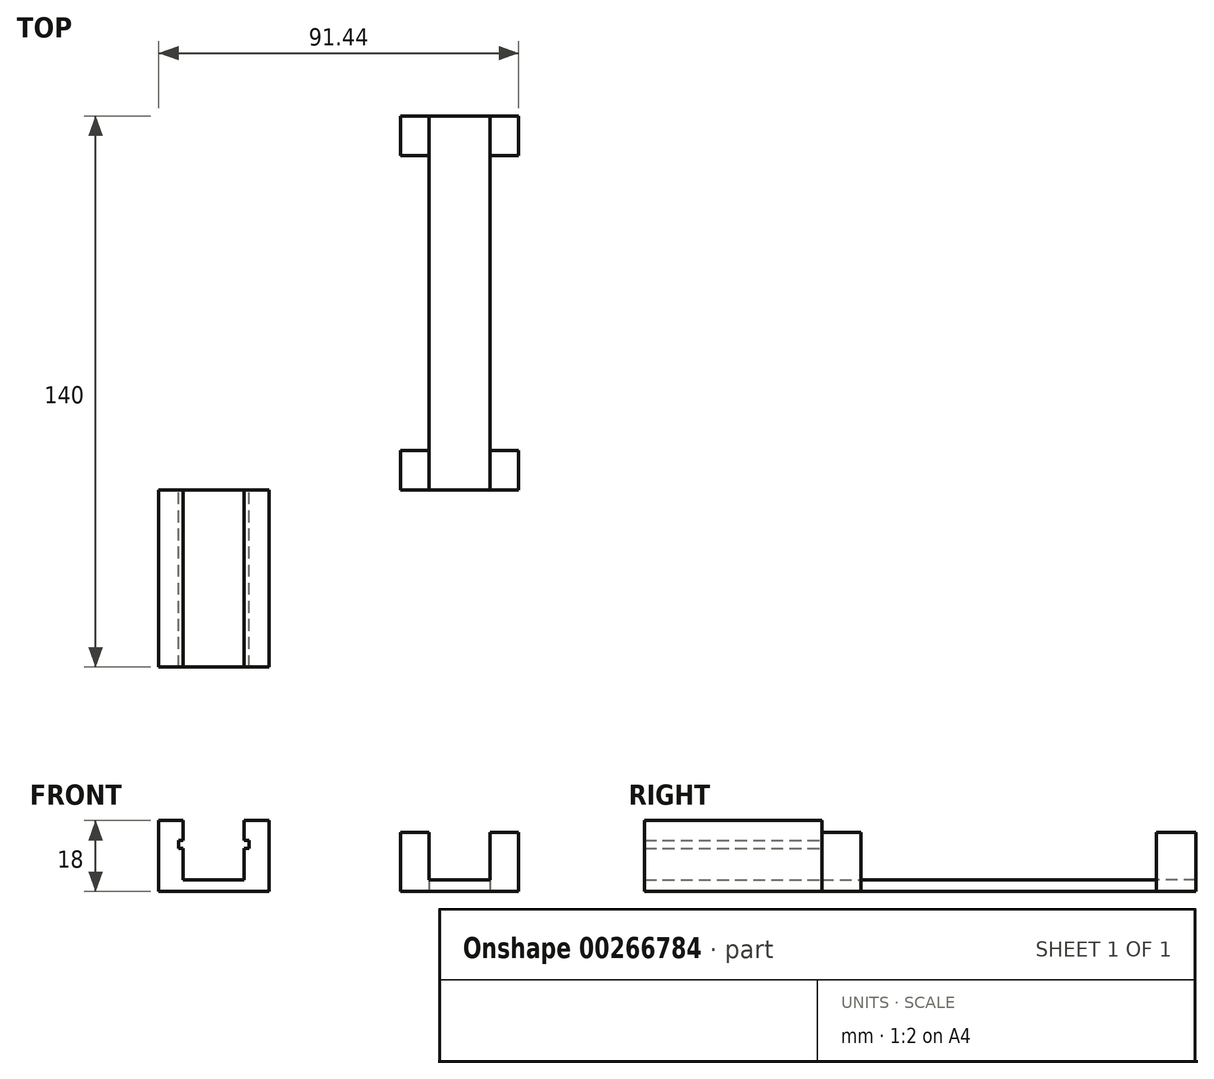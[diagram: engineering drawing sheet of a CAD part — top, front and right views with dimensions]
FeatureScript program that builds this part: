
annotation { "Feature Type Name" : "Feature", "Feature Type Description" : "" }
export const myFeature = defineFeature(function(context is Context, id is Id, definition is map)
    precondition{}
    {
        {
            var Q0;
            Q0=qCreatedBy(makeId("Top.planeOp"),FACE);
            var sketch = newSketch(context, id + "F0", { "sketchPlane" : qUnion([Q0])});
            skLineSegment(sketch, "E0", {"start": v(0, 0) * mm, "end": v(30, 0) * mm});
            skLineSegment(sketch, "E1", {"start": v(30, 0) * mm, "end": v(30, 10) * mm});
            skLineSegment(sketch, "E2", {"start": v(30, 95) * mm, "end": v(0, 95) * mm});
            skLineSegment(sketch, "E3", {"start": v(0, 95) * mm, "end": v(0, 85) * mm});
            skLineSegment(sketch, "E4", {"start": v(7.25, 0) * mm, "end": v(7.25, 10) * mm});
            skLineSegment(sketch, "E5", {"start": v(22.75, 95) * mm, "end": v(22.75, 85) * mm});
            skLineSegment(sketch, "E6", {"start": v(0, 10) * mm, "end": v(7.25, 10) * mm});
            skLineSegment(sketch, "E7", {"start": v(0, 85) * mm, "end": v(7.25, 85) * mm});
            skLineSegment(sketch, "E8.trimOffspring", {"start": v(7.25, 85) * mm, "end": v(7.25, 95) * mm});
            skLineSegment(sketch, "E9.trimOffspring", {"start": v(22.75, 10) * mm, "end": v(22.75, 0) * mm});
            skLineSegment(sketch, "E10.trimOffspring", {"start": v(22.75, 85) * mm, "end": v(30, 85) * mm});
            skLineSegment(sketch, "E11.trimOffspring", {"start": v(22.75, 10) * mm, "end": v(30, 10) * mm});
            skLineSegment(sketch, "E12", {"start": v(7.25, 10) * mm, "end": v(7.25, 85) * mm});
            skLineSegment(sketch, "E13", {"start": v(22.75, 10) * mm, "end": v(22.75, 85) * mm});
            skLineSegment(sketch, "E14.trimOffspring", {"start": v(0, 10) * mm, "end": v(0, 0) * mm});
            skLineSegment(sketch, "E15.trimOffspring", {"start": v(30, 85) * mm, "end": v(30, 95) * mm});
            skSolve(sketch);
        }
        {
            var Q0;
            {var subQ0=sQuery(id+"F0.wireOp",EDGE,"E3");Q0=makeQuery(id+"F0.imprint","IMPRINT",FACE,{"disambiguationData":[TD([[makeQuery(id+"F0.imprint","IMPRINT",EDGE,{"derivedFrom":subQ0}),1.0]])]});}
            var Q1;
            {var subQ0=sQuery(id+"F0.wireOp",EDGE,"E1");Q1=makeQuery(id+"F0.imprint","IMPRINT",FACE,{"disambiguationData":[TD([[makeQuery(id+"F0.imprint","IMPRINT",EDGE,{"derivedFrom":subQ0}),1.0]])]});}
            var Q2;
            {var subQ2=sQuery(id+"F0.wireOp",EDGE,"E5");Q2=makeQuery(id+"F0.imprint","IMPRINT",FACE,{"disambiguationData":[TD([[makeQuery(id+"F0.imprint","IMPRINT",EDGE,{"derivedFrom":subQ2}),1.0]])]});}
            var Q3;
            {var subQ2=sQuery(id+"F0.wireOp",EDGE,"E4");Q3=makeQuery(id+"F0.imprint","IMPRINT",FACE,{"disambiguationData":[TD([[makeQuery(id+"F0.imprint","IMPRINT",EDGE,{"derivedFrom":subQ2}),1.0]])]});}
            extrude(context, id + "F1", {"entities" : qUnion([Q0, Q1, Q2, Q3]), "depth" : 15 * mm});
        }
        {
            var Q0;
            {var subQ0=sQuery(id+"F0.wireOp",EDGE,"E4");Q0=makeQuery(id+"F0.imprint","IMPRINT",FACE,{"disambiguationData":[TD([[makeQuery(id+"F0.imprint","IMPRINT",EDGE,{"derivedFrom":subQ0}),-1.0]])]});}
            extrude(context, id + "F2", {"entities" : qUnion([Q0]), "operationType" : NewBodyOperationType.ADD, "depth" : 3 * mm});
        }
        {
            var Q0;
            Q0=qCreatedBy(makeId("Front.planeOp"),FACE);
            var sketch = newSketch(context, id + "F3", { "sketchPlane" : qUnion([Q0])});
            skLineSegment(sketch, "E16", {"start": v(-61.44, 0) * mm, "end": v(-61.44, 18) * mm});
            skLineSegment(sketch, "E17", {"start": v(-61.44, 18) * mm, "end": v(-55.2, 18) * mm});
            skLineSegment(sketch, "E18", {"start": v(-55.2, 18) * mm, "end": v(-55.2, 13) * mm});
            skLineSegment(sketch, "E19", {"start": v(-55.2, 13) * mm, "end": v(-56.44, 13) * mm});
            skLineSegment(sketch, "E20", {"start": v(-56.44, 13) * mm, "end": v(-56.44, 11) * mm});
            skLineSegment(sketch, "E21", {"start": v(-56.44, 11) * mm, "end": v(-55.2, 11) * mm});
            skLineSegment(sketch, "E22", {"start": v(-55.2, 11) * mm, "end": v(-55.2, 3) * mm});
            skLineSegment(sketch, "E23", {"start": v(-55.2, 3) * mm, "end": v(-39.7, 3) * mm});
            skLineSegment(sketch, "E24", {"start": v(-39.7, 3) * mm, "end": v(-39.7, 11) * mm});
            skLineSegment(sketch, "E25", {"start": v(-39.7, 11) * mm, "end": v(-38.44, 11) * mm});
            skLineSegment(sketch, "E26", {"start": v(-38.44, 11) * mm, "end": v(-38.44, 13) * mm});
            skLineSegment(sketch, "E27", {"start": v(-38.44, 13) * mm, "end": v(-39.7, 13) * mm});
            skLineSegment(sketch, "E28", {"start": v(-39.7, 13) * mm, "end": v(-39.7, 18) * mm});
            skLineSegment(sketch, "E29", {"start": v(-39.7, 18) * mm, "end": v(-33.44, 18) * mm});
            skLineSegment(sketch, "E30", {"start": v(-33.44, 18) * mm, "end": v(-33.44, 0) * mm});
            skLineSegment(sketch, "E31", {"start": v(-33.44, 0) * mm, "end": v(-61.44, 0) * mm});
            skSolve(sketch);
        }
        {
            var Q0;
            Q0=makeQuery(id+"F3.imprint","IMPRINT",FACE,{"disambiguationData":[TD([[makeQuery(id+"F3.imprint","IMPRINT",EDGE,{"derivedFrom":sQuery(id+"F3.wireOp",EDGE,"E16")}),-1.0]])]});
            extrude(context, id + "F4", {"entities" : qUnion([Q0]), "depth" : 45 * mm});
        }
    });
